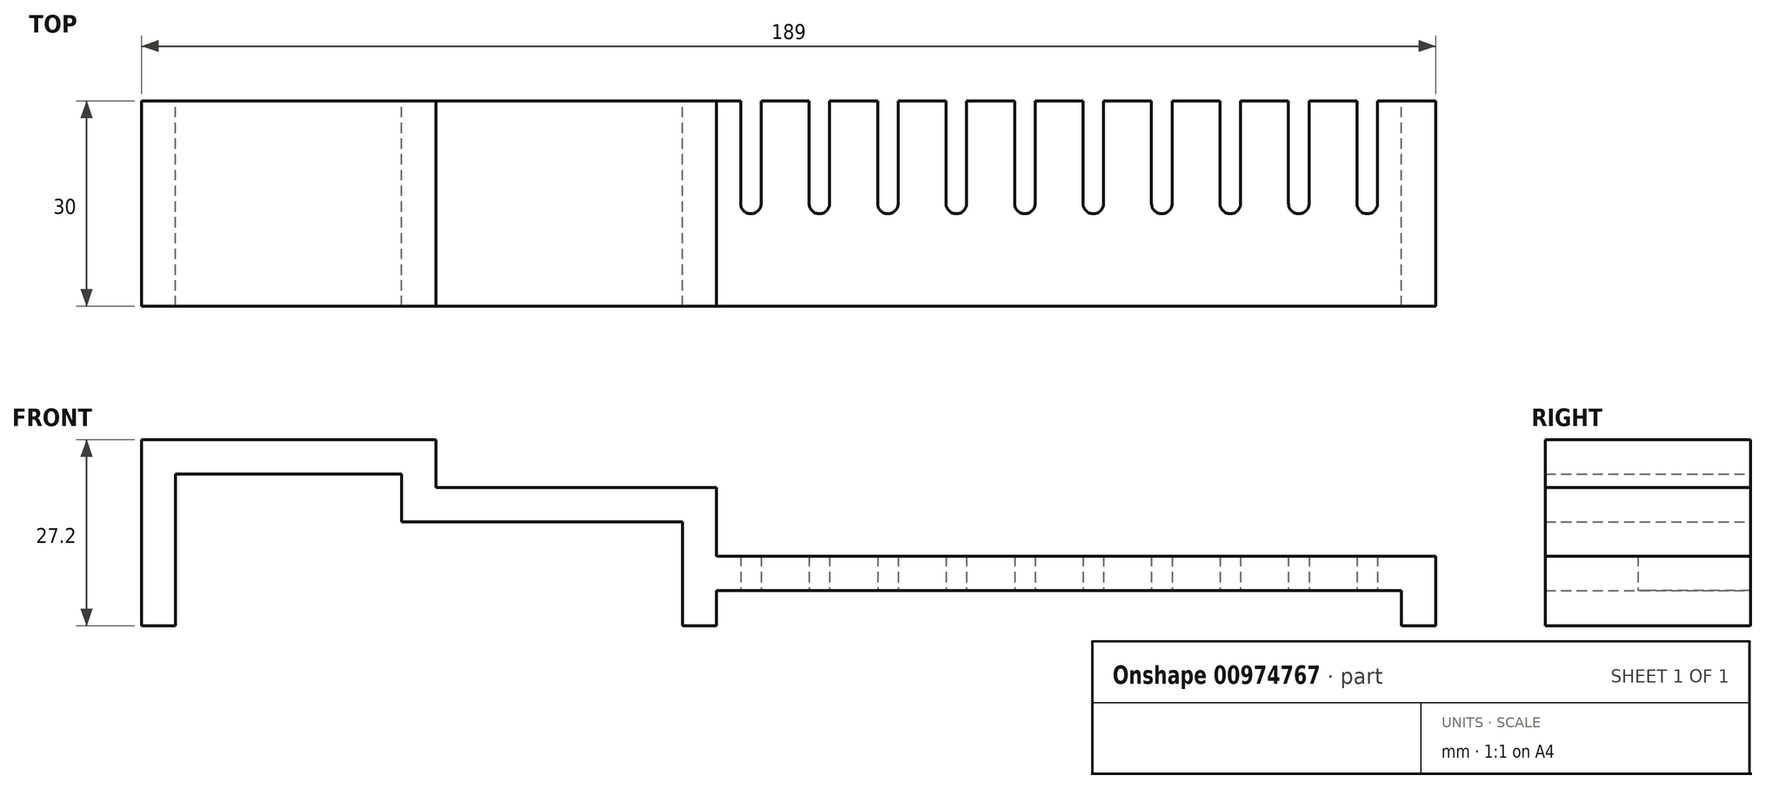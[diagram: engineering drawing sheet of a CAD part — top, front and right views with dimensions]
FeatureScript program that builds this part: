
annotation { "Feature Type Name" : "Feature", "Feature Type Description" : "" }
export const myFeature = defineFeature(function(context is Context, id is Id, definition is map)
    precondition{}
    {
        {
            var Q0;
            Q0=qCreatedBy(makeId("Front.planeOp"),FACE);
            var sketch = newSketch(context, id + "F0", { "sketchPlane" : qUnion([Q0])});
            skLineSegment(sketch, "E0", {"start": v(-33, 0) * mm, "end": v(-33, 22.2) * mm});
            skLineSegment(sketch, "E1", {"start": v(-33, 22.2) * mm, "end": v(0, 22.2) * mm});
            skLineSegment(sketch, "E2", {"start": v(0, 22.2) * mm, "end": v(0, 15.2) * mm});
            skLineSegment(sketch, "E3", {"start": v(0, 15.2) * mm, "end": v(41, 15.2) * mm});
            skLineSegment(sketch, "E4", {"start": v(41, 15.2) * mm, "end": v(41, 0) * mm});
            skLineSegment(sketch, "E5.1", {"start": v(-38, 0) * mm, "end": v(-38, 27.2) * mm});
            skLineSegment(sketch, "E5.2", {"start": v(-38, 27.2) * mm, "end": v(5, 27.2) * mm});
            skLineSegment(sketch, "E5.3", {"start": v(5, 27.2) * mm, "end": v(5, 20.2) * mm});
            skLineSegment(sketch, "E6", {"start": v(-38, 0) * mm, "end": v(-33, 0) * mm});
            skLineSegment(sketch, "E7", {"start": v(5, 20.2) * mm, "end": v(46, 20.2) * mm});
            skLineSegment(sketch, "E8", {"start": v(46, 0) * mm, "end": v(41, 0) * mm});
            skLineSegment(sketch, "E9", {"start": v(46, 10.2) * mm, "end": v(46, 20.2) * mm});
            skLineSegment(sketch, "E10", {"start": v(46, 5.2) * mm, "end": v(46, 0) * mm});
            skLineSegment(sketch, "E11", {"start": v(46, 10.2) * mm, "end": v(151, 10.2) * mm});
            skLineSegment(sketch, "E12", {"start": v(151, 10.2) * mm, "end": v(151, 0) * mm});
            skLineSegment(sketch, "E13.0", {"start": v(146, 5.2) * mm, "end": v(146, 0) * mm});
            skLineSegment(sketch, "E13.1", {"start": v(46, 5.2) * mm, "end": v(146, 5.2) * mm});
            skLineSegment(sketch, "E14", {"start": v(146, 0) * mm, "end": v(151, 0) * mm});
            skLineSegment(sketch, "E15", {"start": v(-33, 0) * mm, "end": v(41, 0) * mm});
            skSolve(sketch);
        }
        {
            var Q0;
            Q0=makeQuery(id+"F0.imprint","IMPRINT",FACE,{"disambiguationData":[TD([[makeQuery(id+"F0.imprint","IMPRINT",EDGE,{"derivedFrom":sQuery(id+"F0.wireOp",EDGE,"E0")}),1.0]])]});
            extrude(context, id + "F1", {"entities" : qUnion([Q0]), "endBound" : BoundingType.SYMMETRIC, "depth" : 30 * mm, "offsetDistance" : 25 * mm});
        }
        {
            var Q0;
            Q0=makeQuery(id+"F1.opExtrude","SWEPT_FACE",FACE,{"disambiguationData":[OSD([sQuery(id+"F0.wireOp",EDGE,"E13.1")])]});
            var sketch = newSketch(context, id + "F2", { "sketchPlane" : qUnion([Q0])});
            skCircle(sketch, "E16", {"center": v(141, 0) * mm, "radius": 1.5 * mm});
            skCircle(sketch, "E17", {"center": v(131, 0) * mm, "radius": 1.5 * mm});
            skCircle(sketch, "E18", {"center": v(121, 0) * mm, "radius": 1.5 * mm});
            skCircle(sketch, "E19", {"center": v(111, 0) * mm, "radius": 1.5 * mm});
            skCircle(sketch, "E20", {"center": v(101, 0) * mm, "radius": 1.5 * mm});
            skCircle(sketch, "E21", {"center": v(91, 0) * mm, "radius": 1.5 * mm});
            skCircle(sketch, "E22", {"center": v(81, 0) * mm, "radius": 1.5 * mm});
            skCircle(sketch, "E23", {"center": v(71, 0) * mm, "radius": 1.5 * mm});
            skCircle(sketch, "E24", {"center": v(61, 0) * mm, "radius": 1.5 * mm});
            skCircle(sketch, "E25", {"center": v(51, 0) * mm, "radius": 1.5 * mm});
            skLineSegment(sketch, "E26", {"start": v(49.5, 0) * mm, "end": v(49.5, -15) * mm});
            skPoint(sketch, "E26.startSnap0", {"position": v(46, 0) * mm});
            skLineSegment(sketch, "E27", {"start": v(59.5, 0) * mm, "end": v(59.5, -15) * mm});
            skLineSegment(sketch, "E28", {"start": v(59.5, -15) * mm, "end": v(62.5, -15) * mm});
            skLineSegment(sketch, "E29", {"start": v(62.5, -15) * mm, "end": v(62.5, 0) * mm});
            skLineSegment(sketch, "E30", {"start": v(69.5, 0) * mm, "end": v(69.5, -15) * mm});
            skLineSegment(sketch, "E31", {"start": v(69.5, -15) * mm, "end": v(72.5, -15) * mm});
            skLineSegment(sketch, "E32", {"start": v(72.5, -15) * mm, "end": v(72.5, 0) * mm});
            skLineSegment(sketch, "E33", {"start": v(79.5, 0) * mm, "end": v(79.5, -15) * mm});
            skLineSegment(sketch, "E34", {"start": v(79.5, -15) * mm, "end": v(82.5, -15) * mm});
            skLineSegment(sketch, "E35", {"start": v(82.5, -15) * mm, "end": v(82.5, 0) * mm});
            skLineSegment(sketch, "E36", {"start": v(89.5, 0) * mm, "end": v(89.5, -15) * mm});
            skLineSegment(sketch, "E37", {"start": v(89.5, -15) * mm, "end": v(92.5, -15) * mm});
            skLineSegment(sketch, "E38", {"start": v(92.5, -15) * mm, "end": v(92.5, 0) * mm});
            skLineSegment(sketch, "E39", {"start": v(99.5, 0) * mm, "end": v(99.5, -15) * mm});
            skLineSegment(sketch, "E40", {"start": v(99.5, -15) * mm, "end": v(102.5, -15) * mm});
            skLineSegment(sketch, "E41", {"start": v(102.5, -15) * mm, "end": v(102.5, 0) * mm});
            skLineSegment(sketch, "E42", {"start": v(109.5, 0) * mm, "end": v(109.5, -15) * mm});
            skLineSegment(sketch, "E43", {"start": v(109.5, -15) * mm, "end": v(112.5, -15) * mm});
            skLineSegment(sketch, "E44", {"start": v(112.5, -15) * mm, "end": v(112.5, 0) * mm});
            skLineSegment(sketch, "E45", {"start": v(119.5, 0) * mm, "end": v(119.5, -15) * mm});
            skLineSegment(sketch, "E46", {"start": v(119.5, -15) * mm, "end": v(122.5, -15) * mm});
            skLineSegment(sketch, "E47", {"start": v(122.5, -15) * mm, "end": v(122.5, 0) * mm});
            skLineSegment(sketch, "E48", {"start": v(49.5, -15) * mm, "end": v(52.5, -15) * mm});
            skLineSegment(sketch, "E49", {"start": v(52.5, -15) * mm, "end": v(52.5, 0) * mm});
            skLineSegment(sketch, "E50", {"start": v(129.5, 0) * mm, "end": v(129.5, -15) * mm});
            skLineSegment(sketch, "E51", {"start": v(129.5, -15) * mm, "end": v(132.5, -15) * mm});
            skLineSegment(sketch, "E52", {"start": v(132.5, -15) * mm, "end": v(132.5, 0) * mm});
            skLineSegment(sketch, "E53", {"start": v(139.5, 0) * mm, "end": v(139.5, -15) * mm});
            skLineSegment(sketch, "E54", {"start": v(139.5, -15) * mm, "end": v(142.5, -15) * mm});
            skLineSegment(sketch, "E55", {"start": v(142.5, -15) * mm, "end": v(142.5, 0) * mm});
            skSolve(sketch);
        }
        {
            var Q0;
            Q0 = qSketchRegion(id + "F2", true);
            extrude(context, id + "F3", {"entities" : qUnion([Q0]), "operationType" : NewBodyOperationType.REMOVE, "oppositeDirection" : true, "depth" : 25 * mm, "offsetDistance" : 25 * mm});
        }
    });
